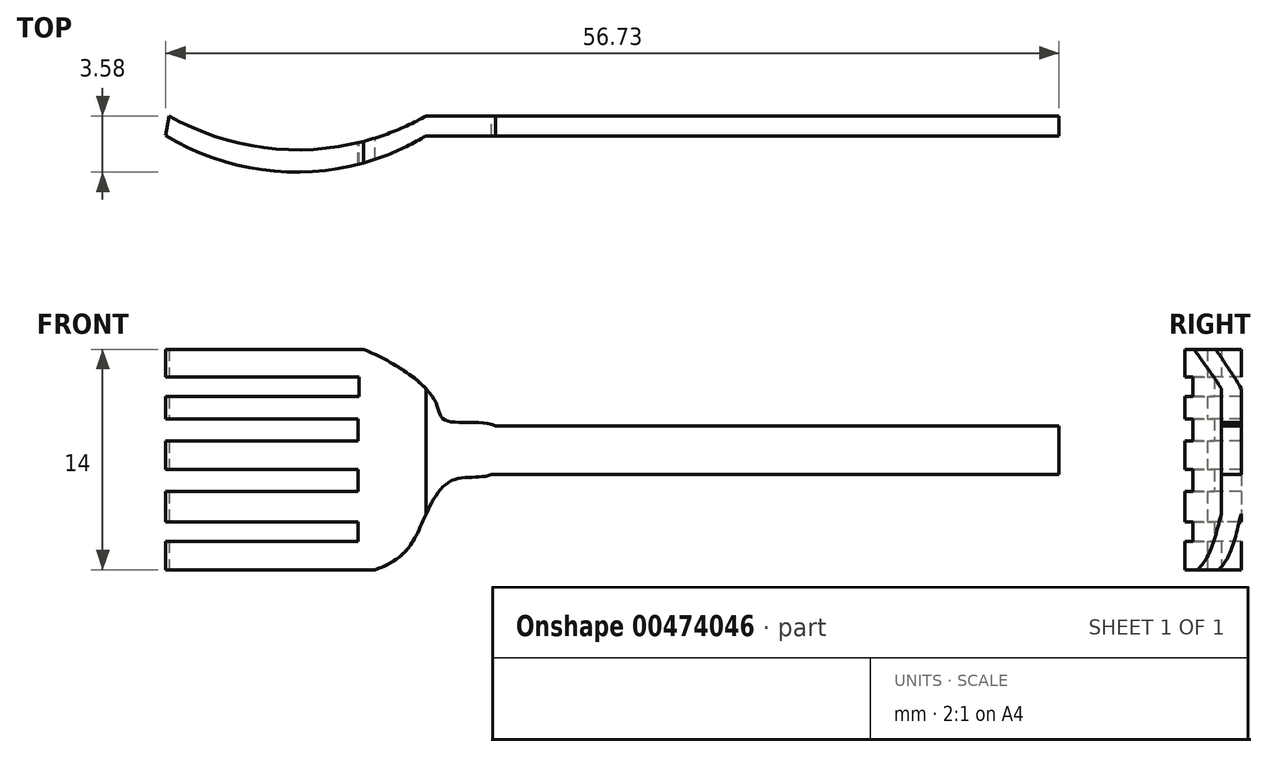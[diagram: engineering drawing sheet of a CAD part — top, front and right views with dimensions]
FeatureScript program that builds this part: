
annotation { "Feature Type Name" : "Feature", "Feature Type Description" : "" }
export const myFeature = defineFeature(function(context is Context, id is Id, definition is map)
    precondition{}
    {
        {
            var Q0;
            Q0=qCreatedBy(makeId("Top.planeOp"),FACE);
            var sketch = newSketch(context, id + "F0", { "sketchPlane" : qUnion([Q0])});
            skLineSegment(sketch, "E0", {"start": v(25.4, -0.14) * mm, "end": v(25.4, -1.41) * mm});
            skLineSegment(sketch, "E1", {"start": v(25.4, -1.41) * mm, "end": v(-14.79, -1.41) * mm});
            skLineSegment(sketch, "E2", {"start": v(25.4, -0.14) * mm, "end": v(-14.78, -0.14) * mm});
            skArc(sketch, "E3", {"start": v(-31.32, -1.4) * mm, "mid": v(-23.06, -3.72) * mm, "end": v(-14.79, -1.41) * mm});
            skArc(sketch, "E4", {"start": v(-31.1, -0.14) * mm, "mid": v(-22.94, -2.3) * mm, "end": v(-14.78, -0.14) * mm});
            skLineSegment(sketch, "E5", {"start": v(-31.1, -0.14) * mm, "end": v(-31.32, -1.4) * mm});
            skSolve(sketch);
        }
        {
            var Q0;
            Q0=makeQuery(id+"F0.imprint","IMPRINT",FACE,{"disambiguationData":[TD([[makeQuery(id+"F0.imprint","IMPRINT",EDGE,{"derivedFrom":sQuery(id+"F0.wireOp",EDGE,"E0")}),-1.0]])]});
            extrude(context, id + "F1", {"entities" : qUnion([Q0]), "depth" : 25.4 * mm});
        }
        {
            var Q0;
            Q0=qCreatedBy(makeId("Front.planeOp"),FACE);
            var sketch = newSketch(context, id + "F2", { "sketchPlane" : qUnion([Q0])});
            skLineSegment(sketch, "E6", {"start": v(26.46, 13.5) * mm, "end": v(-10.37, 13.5) * mm});
            skLineSegment(sketch, "E7", {"start": v(26.2, 10.45) * mm, "end": v(-10.64, 10.45) * mm});
            skLineSegment(sketch, "E8", {"start": v(-14.7, 18.39) * mm, "end": v(-32.14, 18.39) * mm});
            skLineSegment(sketch, "E9", {"start": v(-12.97, 4.39) * mm, "end": v(-31.74, 4.39) * mm});
            skLineSegment(sketch, "E10.bottom", {"start": v(-31.8, 16.62) * mm, "end": v(-19.05, 16.62) * mm});
            skLineSegment(sketch, "E10.top", {"start": v(-31.8, 15.38) * mm, "end": v(-19.05, 15.38) * mm});
            skLineSegment(sketch, "E10.left", {"start": v(-31.8, 16.62) * mm, "end": v(-31.8, 15.38) * mm});
            skLineSegment(sketch, "E10.right", {"start": v(-19.05, 16.62) * mm, "end": v(-19.05, 15.38) * mm});
            skLineSegment(sketch, "E11.bottom", {"start": v(-31.34, 13.97) * mm, "end": v(-19.1, 13.97) * mm});
            skLineSegment(sketch, "E11.top", {"start": v(-31.34, 12.56) * mm, "end": v(-19.1, 12.56) * mm});
            skLineSegment(sketch, "E11.left", {"start": v(-31.34, 13.97) * mm, "end": v(-31.34, 12.56) * mm});
            skLineSegment(sketch, "E11.right", {"start": v(-19.1, 13.97) * mm, "end": v(-19.1, 12.56) * mm});
            skLineSegment(sketch, "E12.bottom", {"start": v(-31.5, 10.76) * mm, "end": v(-19.1, 10.76) * mm});
            skLineSegment(sketch, "E12.top", {"start": v(-31.5, 9.35) * mm, "end": v(-19.1, 9.35) * mm});
            skLineSegment(sketch, "E12.left", {"start": v(-31.5, 10.76) * mm, "end": v(-31.5, 9.35) * mm});
            skLineSegment(sketch, "E12.right", {"start": v(-19.1, 10.76) * mm, "end": v(-19.1, 9.35) * mm});
            skLineSegment(sketch, "E13.bottom", {"start": v(-31.4, 7.44) * mm, "end": v(-19.1, 7.44) * mm});
            skLineSegment(sketch, "E13.top", {"start": v(-31.4, 6.2) * mm, "end": v(-19.1, 6.2) * mm});
            skLineSegment(sketch, "E13.left", {"start": v(-31.4, 7.44) * mm, "end": v(-31.4, 6.2) * mm});
            skLineSegment(sketch, "E13.right", {"start": v(-19.1, 7.44) * mm, "end": v(-19.1, 6.2) * mm});
            skLineSegment(sketch, "E14", {"start": v(-32.14, 18.39) * mm, "end": v(-32.14, 26.47) * mm});
            skLineSegment(sketch, "E15", {"start": v(-32.14, 26.47) * mm, "end": v(26.75, 26.47) * mm});
            skLineSegment(sketch, "E16", {"start": v(26.2, 10.45) * mm, "end": v(26.2, -2.33) * mm});
            skLineSegment(sketch, "E17", {"start": v(26.2, -2.33) * mm, "end": v(-32.14, -2.33) * mm});
            skLineSegment(sketch, "E18", {"start": v(-32.14, -2.33) * mm, "end": v(-31.74, 4.39) * mm});
            skLineSegment(sketch, "E19", {"start": v(26.75, 26.47) * mm, "end": v(26.46, 13.5) * mm});
            skFitSpline(sketch, "E20", {"points": [v(-10.37, 13.5) * mm, v(-13.57, 13.88) * mm, v(-14.25, 15.18) * mm, v(-18.76, 18.39) * mm], "startDerivative": vector(-7.61, 4.13) * mm, "endDerivative": vector(-12.6, 5.08) * mm});
            skFitSpline(sketch, "E21", {"points": [v(-10.64, 10.45) * mm, v(-13.18, 10.05) * mm, v(-15.15, 7.11) * mm, v(-18.02, 4.39) * mm], "startDerivative": vector(-7.22, -3.38) * mm, "endDerivative": vector(-15.12, -5.35) * mm});
            skSolve(sketch);
        }
        {
            var Q0;
            Q0 = qSketchRegion(id + "F2", true);
            extrude(context, id + "F3", {"entities" : qUnion([Q0]), "operationType" : NewBodyOperationType.REMOVE, "endBound" : BoundingType.SYMMETRIC, "depth" : 127 * mm});
        }
    });
